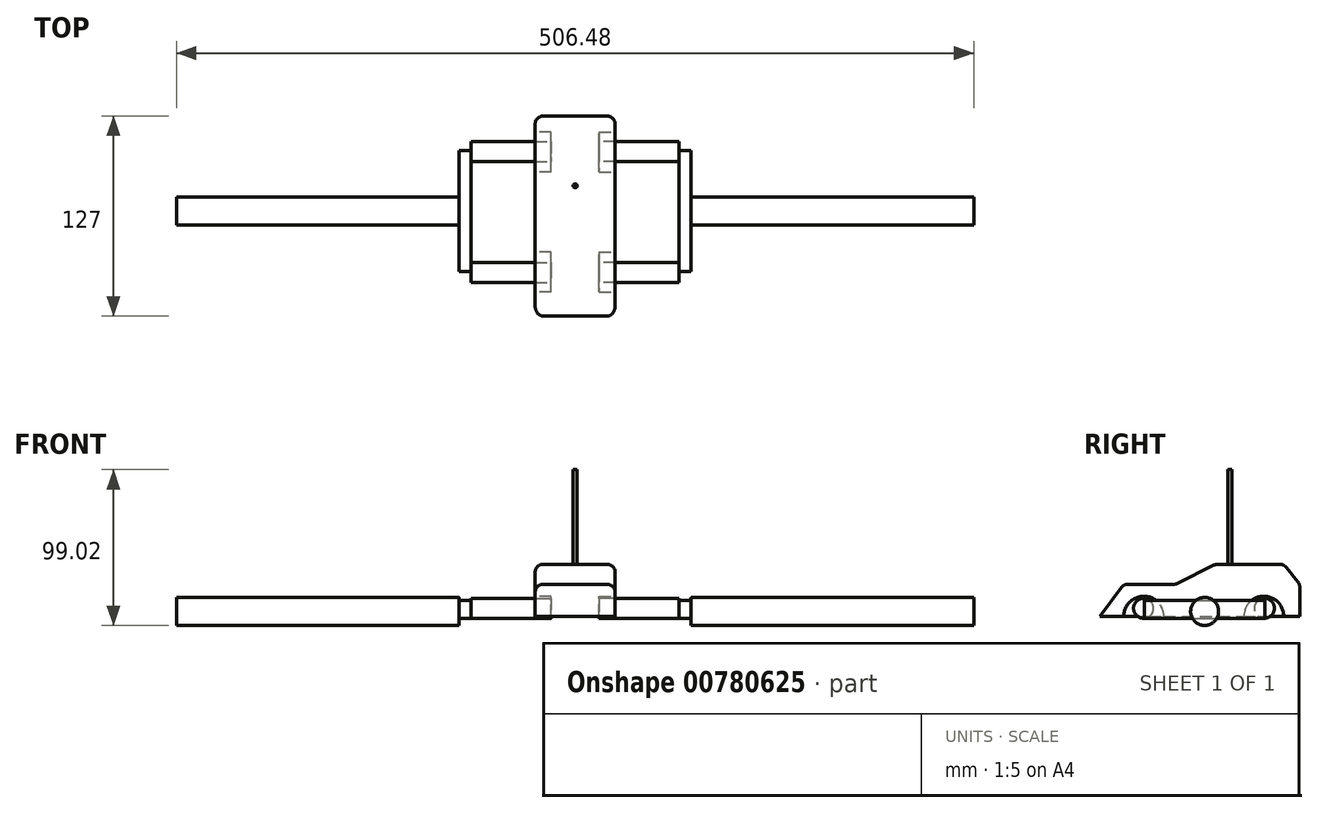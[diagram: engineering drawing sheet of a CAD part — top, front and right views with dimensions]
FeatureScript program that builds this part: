
annotation { "Feature Type Name" : "Feature", "Feature Type Description" : "" }
export const myFeature = defineFeature(function(context is Context, id is Id, definition is map)
    precondition{}
    {
        {
            var Q0;
            Q0=qCreatedBy(makeId("Right.planeOp"),FACE);
            var sketch = newSketch(context, id + "F0", { "sketchPlane" : qUnion([Q0])});
            skLineSegment(sketch, "E0", {"start": v(-76.1, 0) * mm, "end": v(50.9, 0) * mm});
            skLineSegment(sketch, "E1", {"start": v(50.9, 0) * mm, "end": v(50.9, 20.32) * mm});
            skLineSegment(sketch, "E2", {"start": v(50.9, 20.32) * mm, "end": v(40.74, 33.02) * mm});
            skLineSegment(sketch, "E3", {"start": v(40.74, 33.02) * mm, "end": v(-2.44, 33.02) * mm});
            skLineSegment(sketch, "E4", {"start": v(-2.44, 33.02) * mm, "end": v(-27.84, 20.32) * mm});
            skLineSegment(sketch, "E5", {"start": v(-27.84, 20.32) * mm, "end": v(-60.86, 20.32) * mm});
            skLineSegment(sketch, "E6", {"start": v(-60.86, 20.32) * mm, "end": v(-76.1, 0) * mm});
            skSolve(sketch);
        }
        {
            var Q0;
            {var subQ5=sQuery(id+"F0.wireOp",EDGE,"E1");Q0=makeQuery(id+"F0.imprint","IMPRINT",FACE,{"disambiguationData":[TD([[makeQuery(id+"F0.imprint","IMPRINT",EDGE,{"derivedFrom":subQ5}),1.0]])]});}
            var Q1;
            {var subQ0=sQuery(id+"F0.wireOp",EDGE,"XpcTifa5-6JEc-PfwB-YmvP-yD4141RDvFcr");var subQ1=sQuery(id+"F0.wireOp",EDGE,"E0");var subQ2=makeQuery(id+"F0.imprint","INTERSECT",VERTEX,{"disambiguationData":[OD(0.0)],"derivedFrom":[subQ1,subQ0]});Q1=makeQuery(id+"F0.imprint","IMPRINT",FACE,{"disambiguationData":[TD([[makeQuery(id+"F0.imprint","IMPRINT",EDGE,{"disambiguationData":[TD([[subQ2,-1.0]])],"derivedFrom":subQ1}),1.0]])]});}
            var Q2;
            {var subQ0=sQuery(id+"F0.wireOp",EDGE,"0mIZQLD4-nhhb-7qoi-LP5N-WEJVgBk7IHOg");var subQ1=sQuery(id+"F0.wireOp",EDGE,"E0");var subQ2=makeQuery(id+"F0.imprint","INTERSECT",VERTEX,{"disambiguationData":[OD(0.0)],"derivedFrom":[subQ1,subQ0]});Q2=makeQuery(id+"F0.imprint","IMPRINT",FACE,{"disambiguationData":[TD([[makeQuery(id+"F0.imprint","IMPRINT",EDGE,{"disambiguationData":[TD([[subQ2,-1.0]])],"derivedFrom":subQ1}),1.0]])]});}
            extrude(context, id + "F1", {"entities" : qUnion([Q0, Q1, Q2]), "endBound" : BoundingType.SYMMETRIC, "depth" : 50.8 * mm, "offsetDistance" : 25.4 * mm});
        }
        {
            var Q0;
            Q0=makeQuery(id+"F1.opExtrude","CAP_EDGE",EDGE,{"disambiguationData":[OSD([sQuery(id+"F0.wireOp",EDGE,"E6")])],"isStart":false});
            var Q1;
            Q1=makeQuery(id+"F1.opExtrude","CAP_EDGE",EDGE,{"disambiguationData":[OSD([sQuery(id+"F0.wireOp",EDGE,"E5")])],"isStart":false});
            var Q2;
            Q2=makeQuery(id+"F1.opExtrude","CAP_EDGE",EDGE,{"disambiguationData":[OSD([sQuery(id+"F0.wireOp",EDGE,"E4")])],"isStart":false});
            var Q3;
            Q3=makeQuery(id+"F1.opExtrude","CAP_EDGE",EDGE,{"disambiguationData":[OSD([sQuery(id+"F0.wireOp",EDGE,"E3")])],"isStart":false});
            var Q4;
            Q4=makeQuery(id+"F1.opExtrude","CAP_EDGE",EDGE,{"disambiguationData":[OSD([sQuery(id+"F0.wireOp",EDGE,"E2")])],"isStart":false});
            var Q5;
            Q5=makeQuery(id+"F1.opExtrude","CAP_EDGE",EDGE,{"disambiguationData":[OSD([sQuery(id+"F0.wireOp",EDGE,"E1")])],"isStart":false});
            var Q6;
            Q6=makeQuery(id+"F1.opExtrude","SWEPT_EDGE",EDGE,{"disambiguationData":[OSD([sQuery(id+"F0.wireOp",EDGE,"E1"),sQuery(id+"F0.wireOp",EDGE,"E2")])]});
            var Q7;
            Q7=makeQuery(id+"F1.opExtrude","SWEPT_EDGE",EDGE,{"disambiguationData":[OSD([sQuery(id+"F0.wireOp",EDGE,"E2"),sQuery(id+"F0.wireOp",EDGE,"E3")])]});
            var Q8;
            Q8=makeQuery(id+"F1.opExtrude","SWEPT_EDGE",EDGE,{"disambiguationData":[OSD([sQuery(id+"F0.wireOp",EDGE,"E5"),sQuery(id+"F0.wireOp",EDGE,"E6")])]});
            var Q9;
            Q9=makeQuery(id+"F1.opExtrude","SWEPT_EDGE",EDGE,{"disambiguationData":[OSD([sQuery(id+"F0.wireOp",EDGE,"E4"),sQuery(id+"F0.wireOp",EDGE,"E5")])]});
            var Q10;
            Q10=makeQuery(id+"F1.opExtrude","SWEPT_EDGE",EDGE,{"disambiguationData":[OSD([sQuery(id+"F0.wireOp",EDGE,"E3"),sQuery(id+"F0.wireOp",EDGE,"E4")])]});
            var Q11;
            Q11=makeQuery(id+"F1.opExtrude","CAP_EDGE",EDGE,{"disambiguationData":[OSD([sQuery(id+"F0.wireOp",EDGE,"E4")])],"isStart":true});
            var Q12;
            Q12=makeQuery(id+"F1.opExtrude","CAP_EDGE",EDGE,{"disambiguationData":[OSD([sQuery(id+"F0.wireOp",EDGE,"E5")])],"isStart":true});
            var Q13;
            Q13=makeQuery(id+"F1.opExtrude","CAP_EDGE",EDGE,{"disambiguationData":[OSD([sQuery(id+"F0.wireOp",EDGE,"E6")])],"isStart":true});
            var Q14;
            Q14=makeQuery(id+"F1.opExtrude","CAP_EDGE",EDGE,{"disambiguationData":[OSD([sQuery(id+"F0.wireOp",EDGE,"E3")])],"isStart":true});
            var Q15;
            Q15=makeQuery(id+"F1.opExtrude","CAP_EDGE",EDGE,{"disambiguationData":[OSD([sQuery(id+"F0.wireOp",EDGE,"E1")])],"isStart":true});
            var Q16;
            Q16=makeQuery(id+"F1.opExtrude","CAP_EDGE",EDGE,{"disambiguationData":[OSD([sQuery(id+"F0.wireOp",EDGE,"E2")])],"isStart":true});
            fillet(context, id + "F2", {"entities" : qUnion([Q0, Q1, Q2, Q3, Q4, Q5, Q6, Q7, Q8, Q9, Q10, Q11, Q12, Q13, Q14, Q15, Q16]), "radius" : 5.08 * mm, "tangentPropagation" : true, "allowEdgeOverflow" : false});
        }
        {
            var Q0;
            Q0=makeQuery(id+"F1.opExtrude","CAP_FACE",FACE,{"disambiguationData":[OSD([sQuery(id+"F0.wireOp",EDGE,"E0"),sQuery(id+"F0.wireOp",EDGE,"E1"),sQuery(id+"F0.wireOp",EDGE,"E2"),sQuery(id+"F0.wireOp",EDGE,"E3"),sQuery(id+"F0.wireOp",EDGE,"E4"),sQuery(id+"F0.wireOp",EDGE,"E5"),sQuery(id+"F0.wireOp",EDGE,"E6")])],"isStart":false});
            var sketch = newSketch(context, id + "F3", { "sketchPlane" : qUnion([Q0])});
            skCircle(sketch, "E7", {"center": v(-48.16, 0) * mm, "radius": 12.7 * mm});
            skCircle(sketch, "E8", {"center": v(28.04, 0) * mm, "radius": 12.7 * mm});
            skSolve(sketch);
        }
        {
            var Q0;
            {var subQ0=sQuery(id+"F3.wireOp",EDGE,"E7");var subQ1=makeQuery(id+"F1.opExtrude","CAP_EDGE",EDGE,{"disambiguationData":[OSD([sQuery(id+"F0.wireOp",EDGE,"E0")])],"isStart":false});var subQ2=makeQuery(id+"F3.imprint","INTERSECT",VERTEX,{"disambiguationData":[OD(0.0)],"derivedFrom":[subQ1,subQ0]});Q0=makeQuery(id+"F3.imprint","IMPRINT",FACE,{"disambiguationData":[TD([[makeQuery(id+"F3.imprint","IMPRINT",EDGE,{"disambiguationData":[TD([[subQ2,1.0]])],"derivedFrom":subQ0}),1.0]])]});}
            var Q1;
            {var subQ0=sQuery(id+"F3.wireOp",EDGE,"E8");var subQ1=makeQuery(id+"F1.opExtrude","CAP_EDGE",EDGE,{"disambiguationData":[OSD([sQuery(id+"F0.wireOp",EDGE,"E0")])],"isStart":false});var subQ2=makeQuery(id+"F3.imprint","INTERSECT",VERTEX,{"disambiguationData":[OD(0.0)],"derivedFrom":[subQ1,subQ0]});Q1=makeQuery(id+"F3.imprint","IMPRINT",FACE,{"disambiguationData":[TD([[makeQuery(id+"F3.imprint","IMPRINT",EDGE,{"disambiguationData":[TD([[subQ2,-1.0]])],"derivedFrom":subQ0}),1.0]])]});}
            extrude(context, id + "F4", {"entities" : qUnion([Q0, Q1]), "operationType" : NewBodyOperationType.REMOVE, "oppositeDirection" : true, "depth" : 10.16 * mm, "offsetDistance" : 25.4 * mm});
        }
        {
            var Q0;
            Q0=makeQuery(id+"F1.opExtrude","CAP_FACE",FACE,{"disambiguationData":[OSD([sQuery(id+"F0.wireOp",EDGE,"E0"),sQuery(id+"F0.wireOp",EDGE,"E1"),sQuery(id+"F0.wireOp",EDGE,"E2"),sQuery(id+"F0.wireOp",EDGE,"E3"),sQuery(id+"F0.wireOp",EDGE,"E4"),sQuery(id+"F0.wireOp",EDGE,"E5"),sQuery(id+"F0.wireOp",EDGE,"E6")])],"isStart":true});
            var sketch = newSketch(context, id + "F5", { "sketchPlane" : qUnion([Q0])});
            skCircle(sketch, "E9", {"center": v(48.16, 0) * mm, "radius": 12.7 * mm});
            skCircle(sketch, "E10", {"center": v(-28.04, 0) * mm, "radius": 12.7 * mm});
            skSolve(sketch);
        }
        {
            var Q0;
            {var subQ0=sQuery(id+"F5.wireOp",EDGE,"E10");var subQ1=makeQuery(id+"F1.opExtrude","CAP_EDGE",EDGE,{"disambiguationData":[OSD([sQuery(id+"F0.wireOp",EDGE,"E0")])],"isStart":true});var subQ2=makeQuery(id+"F5.imprint","INTERSECT",VERTEX,{"disambiguationData":[OD(0.0)],"derivedFrom":[subQ1,subQ0]});Q0=makeQuery(id+"F5.imprint","IMPRINT",FACE,{"disambiguationData":[TD([[makeQuery(id+"F5.imprint","IMPRINT",EDGE,{"disambiguationData":[TD([[subQ2,1.0]])],"derivedFrom":subQ0}),1.0]])]});}
            var Q1;
            {var subQ0=sQuery(id+"F5.wireOp",EDGE,"E9");var subQ1=makeQuery(id+"F1.opExtrude","CAP_EDGE",EDGE,{"disambiguationData":[OSD([sQuery(id+"F0.wireOp",EDGE,"E0")])],"isStart":true});var subQ2=makeQuery(id+"F5.imprint","INTERSECT",VERTEX,{"disambiguationData":[OD(0.0)],"derivedFrom":[subQ1,subQ0]});Q1=makeQuery(id+"F5.imprint","IMPRINT",FACE,{"disambiguationData":[TD([[makeQuery(id+"F5.imprint","IMPRINT",EDGE,{"disambiguationData":[TD([[subQ2,-1.0]])],"derivedFrom":subQ0}),1.0]])]});}
            extrude(context, id + "F6", {"entities" : qUnion([Q0, Q1]), "operationType" : NewBodyOperationType.REMOVE, "oppositeDirection" : true, "depth" : 10.16 * mm, "offsetDistance" : 25.4 * mm});
        }
        {
            var Q0;
            Q0=makeQuery(id+"F4.boolean.opBoolean","COPY",FACE,{"derivedFrom":makeQuery(id+"F4.opExtrude","CAP_FACE",FACE,{"disambiguationData":[OSD([sQuery(id+"F0.wireOp",EDGE,"E0"),sQuery(id+"F3.wireOp",EDGE,"E8")])],"isStart":false})});
            var sketch = newSketch(context, id + "F7", { "sketchPlane" : qUnion([Q0])});
            skCircle(sketch, "E11", {"center": v(-48.37, 5.08) * mm, "radius": 6.35 * mm});
            skCircle(sketch, "E12", {"center": v(28.4, 5.08) * mm, "radius": 6.35 * mm});
            skSolve(sketch);
        }
        {
            var Q0;
            {var subQ0=sQuery(id+"F7.wireOp",EDGE,"E12");var subQ1=sQuery(id+"F3.wireOp",EDGE,"E8");var subQ2=sQuery(id+"F0.wireOp",EDGE,"E0");var subQ3=makeQuery(id+"F1.opExtrude","CAP_EDGE",EDGE,{"disambiguationData":[OSD([subQ2])],"isStart":false});var subQ4=makeQuery(id+"F4.boolean.opBoolean","COPY",EDGE,{"derivedFrom":makeQuery(id+"F4.opExtrude","CAP_EDGE",EDGE,{"disambiguationData":[OSD([subQ2]),TDD([makeQuery(id+"F3.imprint","IMPRINT",EDGE,{"disambiguationData":[TD([[makeQuery(id+"F3.imprint","INTERSECT",VERTEX,{"disambiguationData":[OD(0.0)],"derivedFrom":[subQ3,subQ1]}),1.0]])],"derivedFrom":subQ3})])],"isStart":false})});var subQ5=makeQuery(id+"F7.imprint","INTERSECT",VERTEX,{"disambiguationData":[OD(0.0)],"derivedFrom":[subQ4,subQ0]});Q0=makeQuery(id+"F7.imprint","IMPRINT",FACE,{"disambiguationData":[TD([[makeQuery(id+"F7.imprint","IMPRINT",EDGE,{"disambiguationData":[TD([[subQ5,-1.0]])],"derivedFrom":subQ0}),1.0]])]});}
            var Q1;
            Q1=makeQuery(id+"F7.imprint","IMPRINT",FACE,{"disambiguationData":[TD([[makeQuery(id+"F7.imprint","IMPRINT",EDGE,{"derivedFrom":sQuery(id+"F7.wireOp",EDGE,"E11")}),1.0]])]});
            var Q2;
            {var subQ0=sQuery(id+"F7.wireOp",EDGE,"E12");var subQ1=sQuery(id+"F3.wireOp",EDGE,"E8");var subQ2=sQuery(id+"F0.wireOp",EDGE,"E0");var subQ3=makeQuery(id+"F1.opExtrude","CAP_EDGE",EDGE,{"disambiguationData":[OSD([subQ2])],"isStart":false});var subQ4=makeQuery(id+"F4.boolean.opBoolean","COPY",EDGE,{"derivedFrom":makeQuery(id+"F4.opExtrude","CAP_EDGE",EDGE,{"disambiguationData":[OSD([subQ2]),TDD([makeQuery(id+"F3.imprint","IMPRINT",EDGE,{"disambiguationData":[TD([[makeQuery(id+"F3.imprint","INTERSECT",VERTEX,{"disambiguationData":[OD(0.0)],"derivedFrom":[subQ3,subQ1]}),1.0]])],"derivedFrom":subQ3})])],"isStart":false})});var subQ5=makeQuery(id+"F7.imprint","INTERSECT",VERTEX,{"disambiguationData":[OD(0.0)],"derivedFrom":[subQ4,subQ0]});Q2=makeQuery(id+"F7.imprint","IMPRINT",FACE,{"disambiguationData":[TD([[makeQuery(id+"F7.imprint","IMPRINT",EDGE,{"disambiguationData":[TD([[subQ5,1.0]])],"derivedFrom":subQ0}),1.0]])]});}
            extrude(context, id + "F8", {"entities" : qUnion([Q0, Q1, Q2]), "operationType" : NewBodyOperationType.ADD, "depth" : 50.8 * mm, "offsetDistance" : 25.4 * mm});
        }
        {
            var Q0;
            Q0=makeQuery(id+"F1.opExtrude","SWEPT_BODY",BODY,{"disambiguationData":[OSD([sQuery(id+"F0.wireOp",EDGE,"E0"),sQuery(id+"F0.wireOp",EDGE,"E1"),sQuery(id+"F0.wireOp",EDGE,"E2"),sQuery(id+"F0.wireOp",EDGE,"E3"),sQuery(id+"F0.wireOp",EDGE,"E4"),sQuery(id+"F0.wireOp",EDGE,"E5"),sQuery(id+"F0.wireOp",EDGE,"E6")])]});
            var Q1;
            Q1=qCreatedBy(makeId("Right.planeOp"),FACE);
            mirror(context, id + "F9", {"operationType" : NewBodyOperationType.ADD, "entities" : qUnion([Q0]), "mirrorPlane" : qUnion([Q1])});
        }
        {
            var Q0;
            Q0=makeQuery(id+"F8.opExtrude","CAP_FACE",FACE,{"disambiguationData":[OSD([sQuery(id+"F7.wireOp",EDGE,"E12")])],"isStart":false});
            var sketch = newSketch(context, id + "F10", { "sketchPlane" : qUnion([Q0])});
            skLineSegment(sketch, "E13.bottom", {"start": v(-47.95, -1.27) * mm, "end": v(28.86, -1.27) * mm});
            skLineSegment(sketch, "E13.top", {"start": v(-47.95, 10.14) * mm, "end": v(28.86, 10.14) * mm});
            skLineSegment(sketch, "E13.left", {"start": v(-47.95, -1.27) * mm, "end": v(-47.95, 10.14) * mm});
            skLineSegment(sketch, "E13.right", {"start": v(28.86, -1.27) * mm, "end": v(28.86, 10.14) * mm});
            skSolve(sketch);
        }
        {
            var Q0;
            Q0 = qSketchRegion(id + "F10", true);
            extrude(context, id + "F11", {"entities" : qUnion([Q0]), "operationType" : NewBodyOperationType.ADD, "depth" : 7.62 * mm, "offsetDistance" : 25.4 * mm});
        }
        {
            var Q0;
            Q0=makeQuery(id+"F1.opExtrude","SWEPT_BODY",BODY,{"disambiguationData":[OSD([sQuery(id+"F0.wireOp",EDGE,"E0"),sQuery(id+"F0.wireOp",EDGE,"E1"),sQuery(id+"F0.wireOp",EDGE,"E2"),sQuery(id+"F0.wireOp",EDGE,"E3"),sQuery(id+"F0.wireOp",EDGE,"E4"),sQuery(id+"F0.wireOp",EDGE,"E5"),sQuery(id+"F0.wireOp",EDGE,"E6")])]});
            var Q1;
            Q1=qCreatedBy(makeId("Right.planeOp"),FACE);
            mirror(context, id + "F12", {"operationType" : NewBodyOperationType.ADD, "entities" : qUnion([Q0]), "mirrorPlane" : qUnion([Q1])});
        }
        {
            var Q0;
            Q0=makeQuery(id+"F11.opExtrude","CAP_FACE",FACE,{"disambiguationData":[OSD([sQuery(id+"F10.wireOp",EDGE,"E13.bottom"),sQuery(id+"F10.wireOp",EDGE,"E13.top"),sQuery(id+"F10.wireOp",EDGE,"E13.left"),sQuery(id+"F10.wireOp",EDGE,"E13.right")])],"isStart":false});
            var sketch = newSketch(context, id + "F13", { "sketchPlane" : qUnion([Q0])});
            skCircle(sketch, "E14", {"center": v(-9.55, 3.1) * mm, "radius": 8.9 * mm});
            skSolve(sketch);
        }
        {
            var Q0;
            Q0 = qSketchRegion(id + "F13", true);
            extrude(context, id + "F14", {"entities" : qUnion([Q0]), "operationType" : NewBodyOperationType.ADD, "depth" : 179.58 * mm, "offsetDistance" : 25.4 * mm});
        }
        {
            var Q0;
            Q0=makeQuery(id+"F1.opExtrude","SWEPT_BODY",BODY,{"disambiguationData":[OSD([sQuery(id+"F0.wireOp",EDGE,"E0"),sQuery(id+"F0.wireOp",EDGE,"E1"),sQuery(id+"F0.wireOp",EDGE,"E2"),sQuery(id+"F0.wireOp",EDGE,"E3"),sQuery(id+"F0.wireOp",EDGE,"E4"),sQuery(id+"F0.wireOp",EDGE,"E5"),sQuery(id+"F0.wireOp",EDGE,"E6")])]});
            var Q1;
            Q1=qCreatedBy(makeId("Right.planeOp"),FACE);
            mirror(context, id + "F15", {"operationType" : NewBodyOperationType.ADD, "entities" : qUnion([Q0]), "mirrorPlane" : qUnion([Q1])});
        }
        {
            var Q0;
            Q0=makeQuery(id+"F1.opExtrude","SWEPT_FACE",FACE,{"disambiguationData":[OSD([sQuery(id+"F0.wireOp",EDGE,"E3")])]});
            var sketch = newSketch(context, id + "F16", { "sketchPlane" : qUnion([Q0])});
            skCircle(sketch, "E15", {"center": v(0, 6.62) * mm, "radius": 1.27 * mm});
            skSolve(sketch);
        }
        {
            var Q0;
            Q0 = qSketchRegion(id + "F16", true);
            extrude(context, id + "F17", {"entities" : qUnion([Q0]), "operationType" : NewBodyOperationType.ADD, "depth" : 60.2 * mm, "offsetDistance" : 25.4 * mm});
        }
    });
